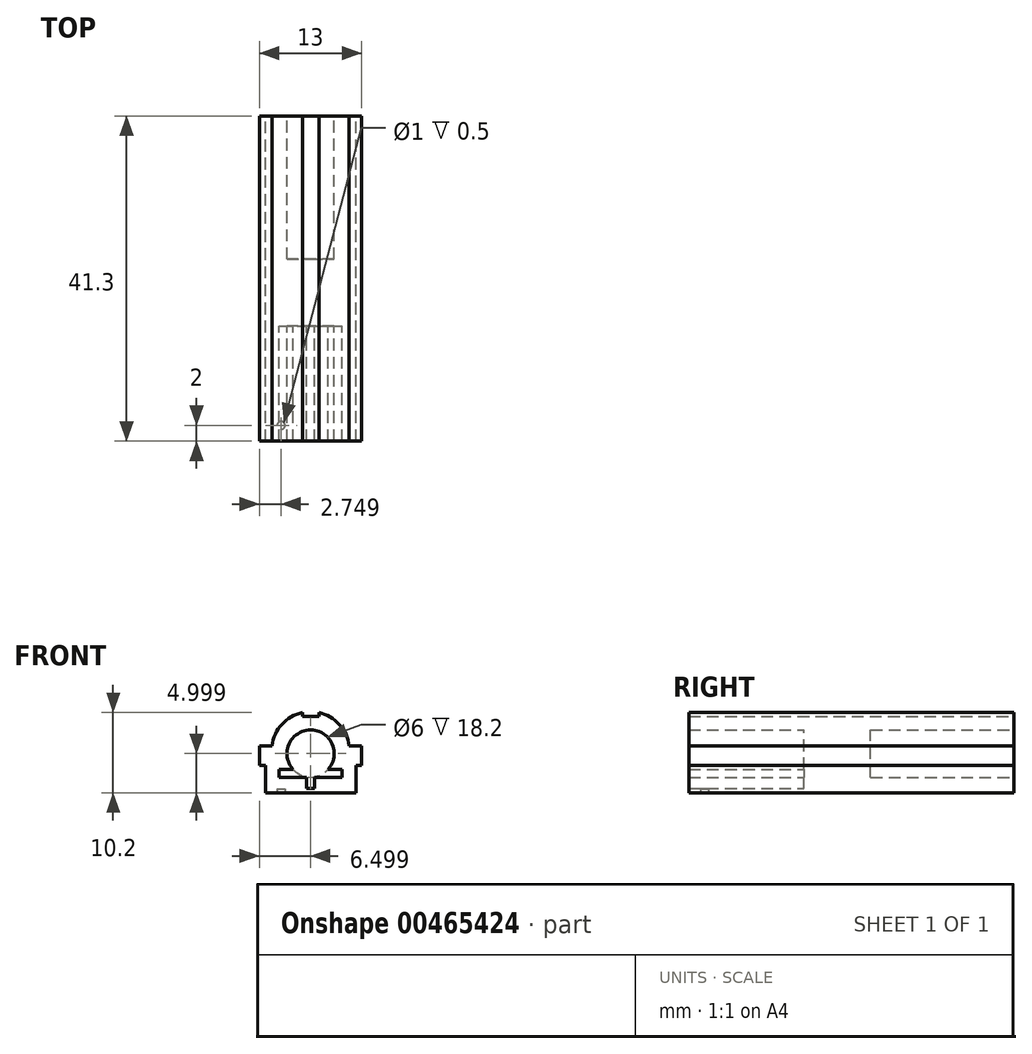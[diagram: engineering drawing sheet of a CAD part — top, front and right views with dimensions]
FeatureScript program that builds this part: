
annotation { "Feature Type Name" : "Feature", "Feature Type Description" : "" }
export const myFeature = defineFeature(function(context is Context, id is Id, definition is map)
    precondition{}
    {
        {
            var Q0;
            Q0=qCreatedBy(makeId("Front.planeOp"),FACE);
            var sketch = newSketch(context, id + "F0", { "sketchPlane" : qUnion([Q0])});
            skLineSegment(sketch, "E0", {"start": v(-15.1, -30.91) * mm, "end": v(-3.6, -30.91) * mm});
            skLineSegment(sketch, "E1", {"start": v(-15.1, -30.91) * mm, "end": v(-15.1, -27.41) * mm});
            skLineSegment(sketch, "E2", {"start": v(-3.6, -30.91) * mm, "end": v(-3.6, -27.41) * mm});
            skLineSegment(sketch, "E3", {"start": v(-15.1, -27.41) * mm, "end": v(-15.84, -27.41) * mm});
            skLineSegment(sketch, "E4", {"start": v(-15.84, -27.41) * mm, "end": v(-15.84, -24.91) * mm});
            skLineSegment(sketch, "E5", {"start": v(-15.84, -24.91) * mm, "end": v(-15.1, -24.91) * mm});
            skLineSegment(sketch, "E6", {"start": v(-3.6, -27.41) * mm, "end": v(-2.84, -27.41) * mm});
            skLineSegment(sketch, "E7", {"start": v(-2.84, -27.41) * mm, "end": v(-2.84, -24.91) * mm});
            skLineSegment(sketch, "E8", {"start": v(-2.84, -24.91) * mm, "end": v(-3.6, -24.91) * mm});
            skLineSegment(sketch, "E9", {"start": v(-8.3, -21.21) * mm, "end": v(-8.3, -20.71) * mm});
            skLineSegment(sketch, "E10", {"start": v(-10.4, -21.21) * mm, "end": v(-10.4, -20.71) * mm});
            skLineSegment(sketch, "E11", {"start": v(-10.4, -21.21) * mm, "end": v(-8.3, -21.21) * mm});
            skCircle(sketch, "E12", {"center": v(-9.34, -25.91) * mm, "radius": 3 * mm});
            skLineSegment(sketch, "E13", {"start": v(-15.1, -24.91) * mm, "end": v(-14.24, -24.91) * mm});
            skLineSegment(sketch, "E14", {"start": v(-3.6, -24.91) * mm, "end": v(-4.44, -24.91) * mm});
            skArc(sketch, "E15", {"start": v(-4.44, -24.91) * mm, "mid": v(-5.7, -22.2) * mm, "end": v(-8.3, -20.71) * mm});
            skArc(sketch, "E16.trimOffspring", {"start": v(-10.4, -20.71) * mm, "mid": v(-12.98, -22.2) * mm, "end": v(-14.24, -24.91) * mm});
            skSolve(sketch);
        }
        {
            var Q0;
            Q0 = qSketchRegion(id + "F0", true);
            extrude(context, id + "F1", {"entities" : qUnion([Q0]), "depth" : 18.2 * mm});
        }
        {
            var Q0;
            Q0=makeQuery(id+"F1.opExtrude","CAP_FACE",FACE,{"disambiguationData":[OSD([sQuery(id+"F0.wireOp",EDGE,"E0"),sQuery(id+"F0.wireOp",EDGE,"E1"),sQuery(id+"F0.wireOp",EDGE,"E2"),sQuery(id+"F0.wireOp",EDGE,"E3"),sQuery(id+"F0.wireOp",EDGE,"E4"),sQuery(id+"F0.wireOp",EDGE,"E5"),sQuery(id+"F0.wireOp",EDGE,"E6"),sQuery(id+"F0.wireOp",EDGE,"E7"),sQuery(id+"F0.wireOp",EDGE,"E8"),sQuery(id+"F0.wireOp",EDGE,"E9"),sQuery(id+"F0.wireOp",EDGE,"E10"),sQuery(id+"F0.wireOp",EDGE,"E11"),sQuery(id+"F0.wireOp",EDGE,"E12"),sQuery(id+"F0.wireOp",EDGE,"E13"),sQuery(id+"F0.wireOp",EDGE,"E14"),sQuery(id+"F0.wireOp",EDGE,"E15"),sQuery(id+"F0.wireOp",EDGE,"E16.trimOffspring")])],"isStart":false});
            var sketch = newSketch(context, id + "F2", { "sketchPlane" : qUnion([Q0])});
            skLineSegment(sketch, "E17", {"start": v(-15.1, -30.91) * mm, "end": v(-3.6, -30.91) * mm});
            skLineSegment(sketch, "E18", {"start": v(-15.1, -30.91) * mm, "end": v(-15.1, -27.41) * mm});
            skLineSegment(sketch, "E19", {"start": v(-3.6, -30.91) * mm, "end": v(-3.6, -27.41) * mm});
            skLineSegment(sketch, "E20", {"start": v(-15.1, -27.41) * mm, "end": v(-15.84, -27.41) * mm});
            skLineSegment(sketch, "E21", {"start": v(-15.84, -27.41) * mm, "end": v(-15.84, -24.91) * mm});
            skLineSegment(sketch, "E22", {"start": v(-15.84, -24.91) * mm, "end": v(-15.1, -24.91) * mm});
            skLineSegment(sketch, "E23", {"start": v(-3.6, -27.41) * mm, "end": v(-2.84, -27.41) * mm});
            skLineSegment(sketch, "E24", {"start": v(-2.84, -27.41) * mm, "end": v(-2.84, -24.91) * mm});
            skLineSegment(sketch, "E25", {"start": v(-2.84, -24.91) * mm, "end": v(-3.6, -24.91) * mm});
            skLineSegment(sketch, "E26", {"start": v(-8.3, -21.21) * mm, "end": v(-8.3, -20.71) * mm});
            skLineSegment(sketch, "E27", {"start": v(-10.4, -21.21) * mm, "end": v(-10.4, -20.71) * mm});
            skLineSegment(sketch, "E28", {"start": v(-10.4, -21.21) * mm, "end": v(-8.3, -21.21) * mm});
            skLineSegment(sketch, "E29", {"start": v(-15.1, -24.91) * mm, "end": v(-14.24, -24.91) * mm});
            skLineSegment(sketch, "E30", {"start": v(-3.6, -24.91) * mm, "end": v(-4.44, -24.91) * mm});
            skArc(sketch, "E31", {"start": v(-4.44, -24.91) * mm, "mid": v(-5.7, -22.2) * mm, "end": v(-8.3, -20.71) * mm});
            skArc(sketch, "E32.trimOffspring", {"start": v(-10.4, -20.71) * mm, "mid": v(-12.98, -22.2) * mm, "end": v(-14.24, -24.91) * mm});
            skSolve(sketch);
        }
        {
            var Q0;
            Q0 = qSketchRegion(id + "F2", true);
            extrude(context, id + "F3", {"entities" : qUnion([Q0]), "operationType" : NewBodyOperationType.ADD, "depth" : 8.5 * mm});
        }
        {
            var Q0;
            Q0=makeQuery(id+"F3.opExtrude","CAP_FACE",FACE,{"disambiguationData":[OSD([sQuery(id+"F2.wireOp",EDGE,"E17"),sQuery(id+"F2.wireOp",EDGE,"E18"),sQuery(id+"F2.wireOp",EDGE,"E19"),sQuery(id+"F2.wireOp",EDGE,"E20"),sQuery(id+"F2.wireOp",EDGE,"E21"),sQuery(id+"F2.wireOp",EDGE,"E22"),sQuery(id+"F2.wireOp",EDGE,"E23"),sQuery(id+"F2.wireOp",EDGE,"E24"),sQuery(id+"F2.wireOp",EDGE,"E25"),sQuery(id+"F2.wireOp",EDGE,"E26"),sQuery(id+"F2.wireOp",EDGE,"E27"),sQuery(id+"F2.wireOp",EDGE,"E28"),sQuery(id+"F2.wireOp",EDGE,"E29"),sQuery(id+"F2.wireOp",EDGE,"E30"),sQuery(id+"F2.wireOp",EDGE,"E31"),sQuery(id+"F2.wireOp",EDGE,"E32.trimOffspring")])],"isStart":false});
            var sketch = newSketch(context, id + "F4", { "sketchPlane" : qUnion([Q0])});
            skLineSegment(sketch, "E33", {"start": v(-15.1, -30.91) * mm, "end": v(-3.6, -30.91) * mm});
            skLineSegment(sketch, "E34", {"start": v(-15.1, -30.91) * mm, "end": v(-15.1, -27.41) * mm});
            skLineSegment(sketch, "E35", {"start": v(-3.6, -30.91) * mm, "end": v(-3.6, -27.41) * mm});
            skLineSegment(sketch, "E36", {"start": v(-15.1, -27.41) * mm, "end": v(-15.84, -27.41) * mm});
            skLineSegment(sketch, "E37", {"start": v(-15.84, -27.41) * mm, "end": v(-15.84, -24.91) * mm});
            skLineSegment(sketch, "E38", {"start": v(-15.84, -24.91) * mm, "end": v(-15.1, -24.91) * mm});
            skLineSegment(sketch, "E39", {"start": v(-3.6, -27.41) * mm, "end": v(-2.84, -27.41) * mm});
            skLineSegment(sketch, "E40", {"start": v(-2.84, -27.41) * mm, "end": v(-2.84, -24.91) * mm});
            skLineSegment(sketch, "E41", {"start": v(-2.84, -24.91) * mm, "end": v(-3.6, -24.91) * mm});
            skLineSegment(sketch, "E42", {"start": v(-8.3, -21.21) * mm, "end": v(-8.3, -20.71) * mm});
            skLineSegment(sketch, "E43", {"start": v(-10.4, -21.21) * mm, "end": v(-10.4, -20.71) * mm});
            skLineSegment(sketch, "E44", {"start": v(-10.4, -21.21) * mm, "end": v(-8.3, -21.21) * mm});
            skArc(sketch, "E45", {"start": v(-7.1, -27.91) * mm, "mid": v(-9.34, -22.91) * mm, "end": v(-11.58, -27.91) * mm});
            skLineSegment(sketch, "E46", {"start": v(-15.1, -24.91) * mm, "end": v(-14.24, -24.91) * mm});
            skLineSegment(sketch, "E47", {"start": v(-3.6, -24.91) * mm, "end": v(-4.44, -24.91) * mm});
            skArc(sketch, "E48", {"start": v(-4.44, -24.91) * mm, "mid": v(-5.7, -22.2) * mm, "end": v(-8.3, -20.71) * mm});
            skArc(sketch, "E49.trimOffspring", {"start": v(-10.4, -20.71) * mm, "mid": v(-12.98, -22.2) * mm, "end": v(-14.24, -24.91) * mm});
            skLineSegment(sketch, "E50.bottom", {"start": v(-13.34, -27.91) * mm, "end": v(-11.58, -27.91) * mm});
            skLineSegment(sketch, "E50.top", {"start": v(-13.34, -28.91) * mm, "end": v(-9.84, -28.91) * mm});
            skLineSegment(sketch, "E50.left", {"start": v(-13.34, -27.91) * mm, "end": v(-13.34, -28.91) * mm});
            skLineSegment(sketch, "E50.right", {"start": v(-5.34, -27.91) * mm, "end": v(-5.34, -28.91) * mm});
            skLineSegment(sketch, "E51", {"start": v(-9.84, -28.91) * mm, "end": v(-9.84, -30.31) * mm});
            skLineSegment(sketch, "E52", {"start": v(-9.84, -30.31) * mm, "end": v(-8.84, -30.31) * mm});
            skLineSegment(sketch, "E53", {"start": v(-8.84, -30.31) * mm, "end": v(-8.84, -28.91) * mm});
            skLineSegment(sketch, "E54.trimOffspring", {"start": v(-7.1, -27.91) * mm, "end": v(-5.34, -27.91) * mm});
            skLineSegment(sketch, "E55.trimOffspring", {"start": v(-8.84, -28.91) * mm, "end": v(-5.34, -28.91) * mm});
            skSolve(sketch);
        }
        {
            var Q0;
            Q0=makeQuery(id+"F4.imprint","IMPRINT",FACE,{"disambiguationData":[TD([[makeQuery(id+"F4.imprint","IMPRINT",EDGE,{"derivedFrom":sQuery(id+"F4.wireOp",EDGE,"E33")}),1.0]])]});
            extrude(context, id + "F5", {"entities" : qUnion([Q0]), "operationType" : NewBodyOperationType.ADD, "depth" : 14.6 * mm});
        }
        {
            var Q0;
            Q0=makeQuery(id+"F5.boolean.opBoolean","MERGE",FACE,{"derivedFrom":[makeQuery(id+"F3.boolean.opBoolean","MERGE",FACE,{"derivedFrom":[makeQuery(id+"F1.opExtrude","SWEPT_FACE",FACE,{"disambiguationData":[OSD([sQuery(id+"F0.wireOp",EDGE,"E0")])]}),makeQuery(id+"F3.opExtrude","SWEPT_FACE",FACE,{"disambiguationData":[OSD([sQuery(id+"F2.wireOp",EDGE,"E17")])]})]}),makeQuery(id+"F5.opExtrude","SWEPT_FACE",FACE,{"disambiguationData":[OSD([sQuery(id+"F4.wireOp",EDGE,"E33")])]})]});
            var sketch = newSketch(context, id + "F6", { "sketchPlane" : qUnion([Q0])});
            skCircle(sketch, "E56", {"center": v(-13.1, 39.3) * mm, "radius": 0.5 * mm});
            skSolve(sketch);
        }
        {
            var Q0;
            Q0=makeQuery(id+"F6.imprint","IMPRINT",FACE,{"disambiguationData":[TD([[makeQuery(id+"F6.imprint","IMPRINT",EDGE,{"derivedFrom":sQuery(id+"F6.wireOp",EDGE,"E56")}),1.0]])]});
            extrude(context, id + "F7", {"entities" : qUnion([Q0]), "operationType" : NewBodyOperationType.REMOVE, "oppositeDirection" : true, "depth" : 0.5 * mm, "offsetDistance" : 25 * mm});
        }
    });
